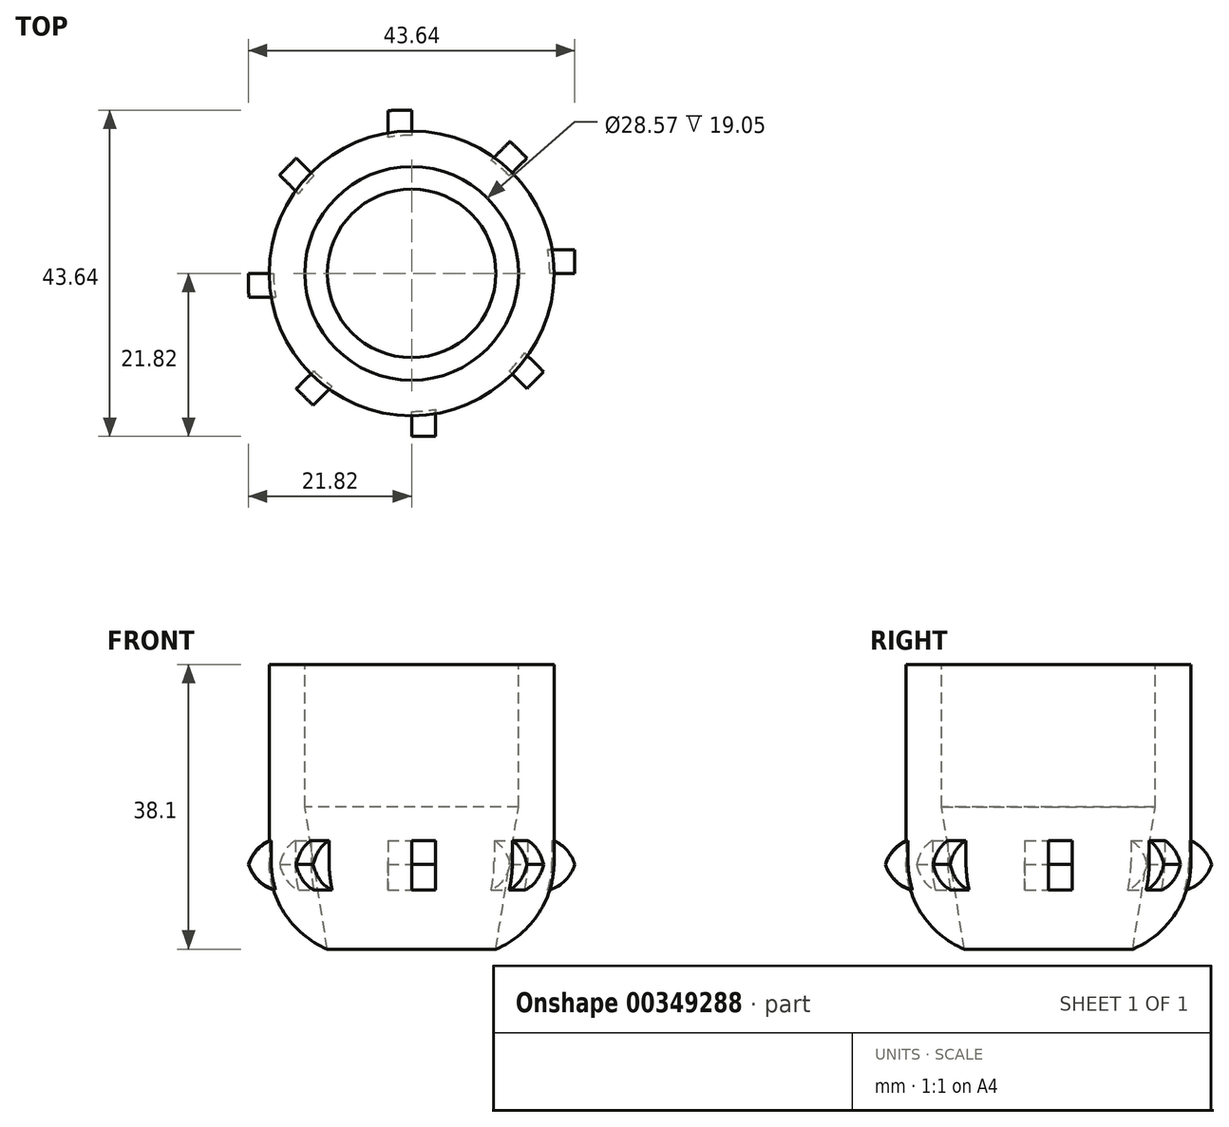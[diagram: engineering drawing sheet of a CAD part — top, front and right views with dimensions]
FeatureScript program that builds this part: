
annotation { "Feature Type Name" : "Feature", "Feature Type Description" : "" }
export const myFeature = defineFeature(function(context is Context, id is Id, definition is map)
    precondition{}
    {
        {
            var Q0;
            Q0=qCreatedBy(makeId("Top.planeOp"),FACE);
            var sketch = newSketch(context, id + "F0", { "sketchPlane" : qUnion([Q0])});
            skCircle(sketch, "E0", {"center": v(0, 0) * mm, "radius": 19.05 * mm});
            skSolve(sketch);
        }
        {
            var Q0;
            Q0=makeQuery(id+"F0.imprint","IMPRINT",FACE,{"disambiguationData":[TD([[makeQuery(id+"F0.imprint","IMPRINT",EDGE,{"derivedFrom":sQuery(id+"F0.wireOp",EDGE,"E0")}),1.0]])]});
            extrude(context, id + "F1", {"entities" : qUnion([Q0]), "depth" : 38.1 * mm});
        }
        {
            var Q0;
            Q0=makeQuery(id+"F1.opExtrude","CAP_FACE",FACE,{"disambiguationData":[OSD([sQuery(id+"F0.wireOp",EDGE,"E0")])],"isStart":false});
            var sketch = newSketch(context, id + "F2", { "sketchPlane" : qUnion([Q0])});
            skCircle(sketch, "E1", {"center": v(0, 0) * mm, "radius": 15.88 * mm});
            skSolve(sketch);
        }
        {
            var Q0;
            Q0=sQuery(id+"F2.wireOp",VERTEX,"E1.center");
            var Q1;
            Q1=makeQuery(id+"F1.opExtrude","SWEPT_BODY",BODY,{"disambiguationData":[OSD([sQuery(id+"F0.wireOp",EDGE,"E0")])]});
            hole(context, id + "F3", {"style" : HoleStyle.SIMPLE, "endStyle" : HoleEndStyle.THROUGH, "holeDiameter" : 28.57 * mm, "isTappedThrough" : true, "tappedDepth" : 12.7 * mm, "tapClearance" : 3, "locations" : qUnion([Q0]), "scope" : qUnion([Q1])});
        }
        {
            var Q0;
            Q0=qCreatedBy(makeId("Top.planeOp"),FACE);
            var sketch = newSketch(context, id + "F4", { "sketchPlane" : qUnion([Q0])});
            skCircle(sketch, "E2", {"center": v(0, 0) * mm, "radius": 14.29 * mm});
            skSolve(sketch);
        }
        {
            var Q0;
            Q0 = qSketchRegion(id + "F4", true);
            extrude(context, id + "F5", {"entities" : qUnion([Q0]), "operationType" : NewBodyOperationType.ADD, "depth" : 19.05 * mm});
        }
        {
            var Q0;
            Q0=makeQuery(id+"F5.opExtrude","CAP_FACE",FACE,{"disambiguationData":[OSD([sQuery(id+"F4.wireOp",EDGE,"E2")])],"isStart":false});
            extrude(context, id + "F6", {"entities" : qUnion([Q0]), "operationType" : NewBodyOperationType.REMOVE, "oppositeDirection" : true, "depth" : 19.05 * mm, "hasDraft" : true, "draftAngle" : 9 * degree, "draftPullDirection" : true});
        }
        {
            var Q0;
            Q0=makeQuery(id+"F1.opExtrude","CAP_EDGE",EDGE,{"disambiguationData":[OSD([sQuery(id+"F0.wireOp",EDGE,"E0")])],"isStart":true});
            fillet(context, id + "F7", {"entities" : qUnion([Q0]), "radius" : 12.7 * mm, "tangentPropagation" : true, "allowEdgeOverflow" : false});
        }
        {
            var Q0;
            {var subQ0=sQuery(id+"F0.wireOp",EDGE,"E0");Q0=makeQuery(id+"F7.opFillet","BLEND_EDGE",EDGE,{"blendedFrom":[makeQuery(id+"F1.opExtrude","CAP_EDGE",EDGE,{"disambiguationData":[OSD([subQ0])],"isStart":true}),makeQuery(id+"F1.opExtrude","SWEPT_FACE",FACE,{"disambiguationData":[OSD([subQ0])]})],"blendedInto":[makeQuery(id+"F1.opExtrude","SWEPT_FACE",FACE,{"disambiguationData":[OSD([subQ0])]})]});}
            cPlane(context, id + "F8", {"entities" : qUnion([Q0]), "cplaneType" : CPlaneType.LINE_ANGLE, "offset" : 25.4 * mm, "angle" : 90 * degree, "width" : 152.4 * mm, "height" : 152.4 * mm});
        }
        {
            var Q0;
            Q0=qCreatedBy(id+"F8.planeOp",FACE);
            var sketch = newSketch(context, id + "F9", { "sketchPlane" : qUnion([Q0])});
            skLineSegment(sketch, "E3.bottom", {"start": v(-18.12, 7.93) * mm, "end": v(-22.02, 7.93) * mm});
            skLineSegment(sketch, "E3.top", {"start": v(-18.12, 14.52) * mm, "end": v(-22.02, 14.52) * mm});
            skLineSegment(sketch, "E3.left", {"start": v(-18.12, 7.93) * mm, "end": v(-18.12, 14.52) * mm});
            skLineSegment(sketch, "E3.right", {"start": v(-22.02, 7.93) * mm, "end": v(-22.02, 14.52) * mm});
            skPoint(sketch, "E3.middle", {"position": v(-20.07, 11.23) * mm});
            skSolve(sketch);
        }
        {
            var Q0;
            Q0=makeQuery(id+"F9.imprint","IMPRINT",FACE,{"disambiguationData":[TD([[makeQuery(id+"F9.imprint","IMPRINT",EDGE,{"derivedFrom":sQuery(id+"F9.wireOp",EDGE,"E3.bottom")}),-1.0]])]});
            extrude(context, id + "F10", {"entities" : qUnion([Q0]), "operationType" : NewBodyOperationType.ADD, "depth" : 3.17 * mm});
        }
        {
            var Q0;
            Q0=makeQuery(id+"F10.opExtrude","SWEPT_EDGE",EDGE,{"disambiguationData":[OSD([sQuery(id+"F9.wireOp",EDGE,"E3.bottom"),sQuery(id+"F9.wireOp",EDGE,"E3.right")])]});
            fillet(context, id + "F11", {"entities" : qUnion([Q0]), "radius" : 5.08 * mm, "tangentPropagation" : true, "allowEdgeOverflow" : false});
        }
        {
            var Q0;
            Q0=makeQuery(id+"F10.opExtrude","SWEPT_EDGE",EDGE,{"disambiguationData":[OSD([sQuery(id+"F9.wireOp",EDGE,"E3.top"),sQuery(id+"F9.wireOp",EDGE,"E3.right")])]});
            fillet(context, id + "F12", {"entities" : qUnion([Q0]), "radius" : 5.08 * mm, "tangentPropagation" : true, "allowEdgeOverflow" : false});
        }
        {
            var Q0;
            Q0=makeQuery(id+"F10.opExtrude","CAP_FACE",FACE,{"disambiguationData":[OSD([sQuery(id+"F9.wireOp",EDGE,"E3.bottom"),sQuery(id+"F9.wireOp",EDGE,"E3.top"),sQuery(id+"F9.wireOp",EDGE,"E3.left"),sQuery(id+"F9.wireOp",EDGE,"E3.right")])],"isStart":false});
            var Q1;
            Q1=makeQuery(id+"F11.opFillet","BLEND_FACE",FACE,{"disambiguationData":[OSD([sQuery(id+"F9.wireOp",EDGE,"E3.bottom"),sQuery(id+"F9.wireOp",EDGE,"E3.right")])]});
            var Q2;
            Q2=makeQuery(id+"F12.opFillet","BLEND_FACE",FACE,{"disambiguationData":[OSD([sQuery(id+"F9.wireOp",EDGE,"E3.top"),sQuery(id+"F9.wireOp",EDGE,"E3.right")])]});
            var Q3;
            Q3=makeQuery(id+"F10.opExtrude","CAP_FACE",FACE,{"disambiguationData":[OSD([sQuery(id+"F9.wireOp",EDGE,"E3.bottom"),sQuery(id+"F9.wireOp",EDGE,"E3.top"),sQuery(id+"F9.wireOp",EDGE,"E3.left"),sQuery(id+"F9.wireOp",EDGE,"E3.right")])],"isStart":true});
            var Q4;
            Q4=makeQuery(id+"F1.opExtrude","SWEPT_FACE",FACE,{"disambiguationData":[OSD([sQuery(id+"F0.wireOp",EDGE,"E0")])]});
            circularPattern(context, id + "F13", {"patternType" : PatternType.FACE, "faces" : qUnion([Q0, Q1, Q2, Q3]), "axis" : qUnion([Q4]), "angle" : 360 * degree, "instanceCount" : 8, "equalSpace" : true});
        }
    });
